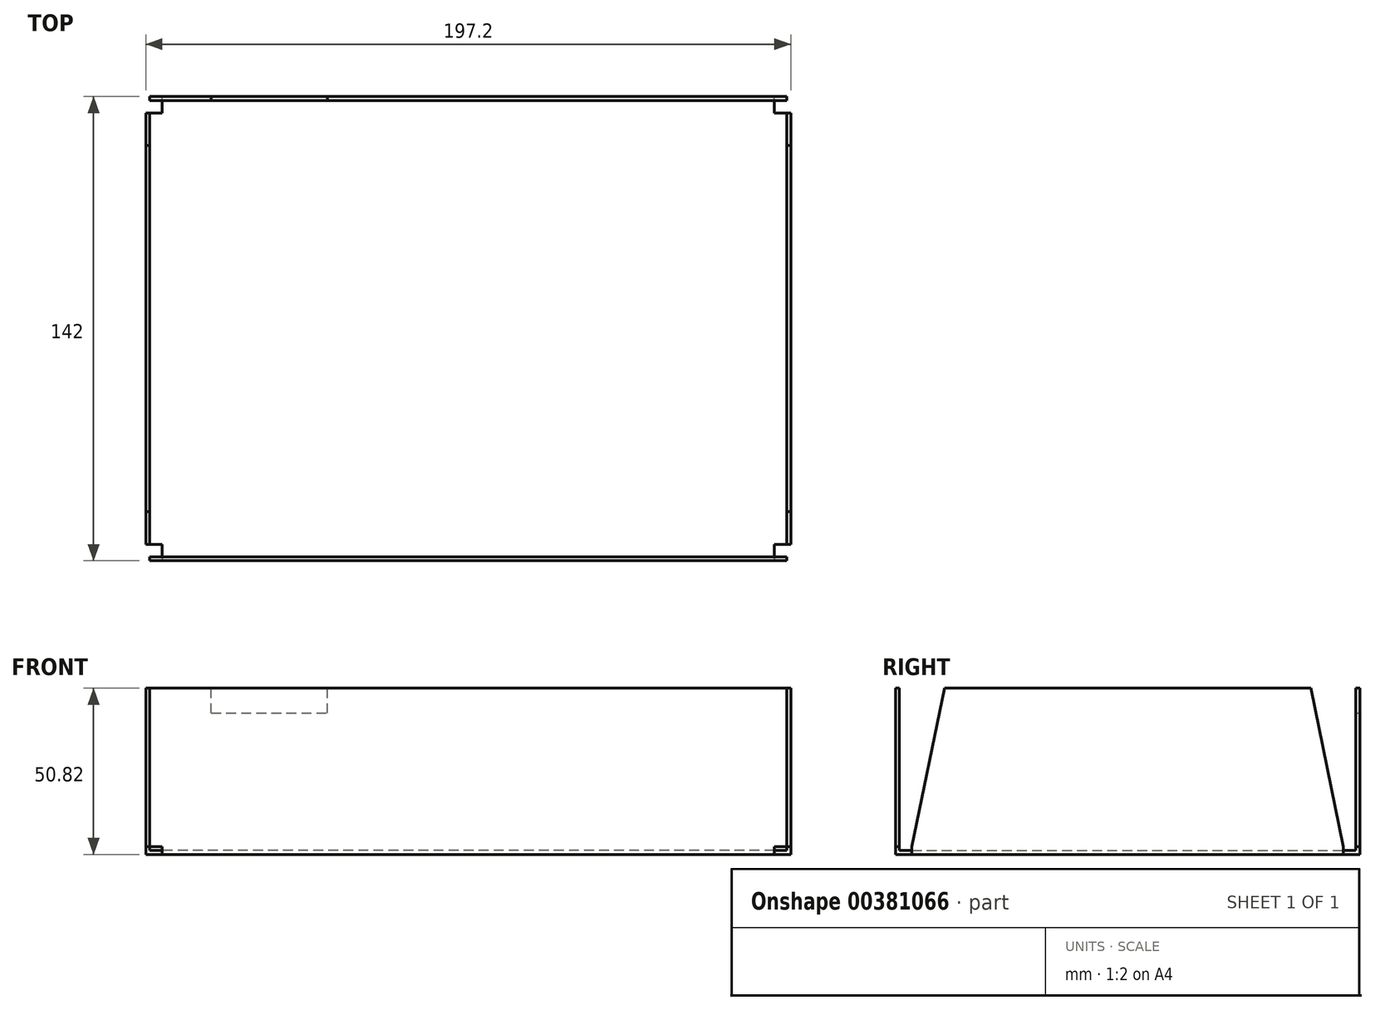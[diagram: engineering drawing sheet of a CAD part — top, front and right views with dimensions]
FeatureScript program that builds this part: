
annotation { "Feature Type Name" : "Feature", "Feature Type Description" : "" }
export const myFeature = defineFeature(function(context is Context, id is Id, definition is map)
    precondition{}
    {
        {
            var Q0;
            Q0=qCreatedBy(makeId("Front.planeOp"),FACE);
            var sketch = newSketch(context, id + "F0", { "sketchPlane" : qUnion([Q0])});
            skLineSegment(sketch, "E0", {"start": v(0, 25.41) * mm, "end": v(-98.6, 25.41) * mm});
            skLineSegment(sketch, "E1", {"start": v(0, 25.41) * mm, "end": v(98.6, 25.41) * mm});
            skLineSegment(sketch, "E2", {"start": v(0, -25.41) * mm, "end": v(-98.6, -25.41) * mm});
            skLineSegment(sketch, "E3", {"start": v(0, -25.41) * mm, "end": v(98.6, -25.41) * mm});
            skLineSegment(sketch, "E4", {"start": v(98.6, 25.41) * mm, "end": v(98.6, -25.41) * mm});
            skLineSegment(sketch, "E5", {"start": v(-98.6, 25.41) * mm, "end": v(-98.6, -25.41) * mm});
            skSolve(sketch);
        }
        {
            var Q0;
            Q0 = qSketchRegion(id + "F0", true);
            extrude(context, id + "F1", {"entities" : qUnion([Q0]), "depth" : 71 * mm, "hasSecondDirection" : true, "secondDirectionOppositeDirection" : true, "secondDirectionDepth" : 71 * mm});
        }
        {
            var Q0;
            Q0=makeQuery(id+"F1.opExtrude","SWEPT_FACE",FACE,{"disambiguationData":[OSD([sQuery(id+"F0.wireOp",EDGE,"E0"),sQuery(id+"F0.wireOp",EDGE,"E1")])]});
            var sketch = newSketch(context, id + "F2", { "sketchPlane" : qUnion([Q0])});
            skLineSegment(sketch, "E6", {"start": v(-97.4, -69.8) * mm, "end": v(-97.4, 69.8) * mm});
            skLineSegment(sketch, "E7", {"start": v(-97.4, 69.8) * mm, "end": v(97.4, 69.8) * mm});
            skLineSegment(sketch, "E8", {"start": v(97.4, 69.8) * mm, "end": v(97.4, -69.8) * mm});
            skLineSegment(sketch, "E9", {"start": v(97.4, -69.8) * mm, "end": v(-97.4, -69.8) * mm});
            skSolve(sketch);
        }
        {
            var Q0;
            Q0 = qSketchRegion(id + "F2", true);
            extrude(context, id + "F3", {"entities" : qUnion([Q0]), "operationType" : NewBodyOperationType.REMOVE, "oppositeDirection" : true, "depth" : (50.82 - 1.2) * mm});
        }
        {
            var Q0;
            Q0=makeQuery(id+"F1.opExtrude","CAP_FACE",FACE,{"disambiguationData":[OSD([sQuery(id+"F0.wireOp",EDGE,"E0"),sQuery(id+"F0.wireOp",EDGE,"E1"),sQuery(id+"F0.wireOp",EDGE,"E2"),sQuery(id+"F0.wireOp",EDGE,"E3"),sQuery(id+"F0.wireOp",EDGE,"E4"),sQuery(id+"F0.wireOp",EDGE,"E5")])],"isStart":true});
            var sketch = newSketch(context, id + "F4", { "sketchPlane" : qUnion([Q0])});
            skLineSegment(sketch, "E10", {"start": v(78.6, 17.8) * mm, "end": v(78.6, 25.41) * mm});
            skLineSegment(sketch, "E11", {"start": v(78.6, 17.8) * mm, "end": v(43.04, 17.8) * mm});
            skLineSegment(sketch, "E12", {"start": v(43.04, 17.8) * mm, "end": v(43.04, 25.41) * mm});
            skSolve(sketch);
        }
        {
            var Q0;
            {var subQ0=sQuery(id+"F4.wireOp",EDGE,"E10");Q0=makeQuery(id+"F4.imprint","IMPRINT",FACE,{"disambiguationData":[TD([[makeQuery(id+"F4.imprint","IMPRINT",EDGE,{"derivedFrom":subQ0}),1.0]])]});}
            extrude(context, id + "F5", {"entities" : qUnion([Q0]), "operationType" : NewBodyOperationType.REMOVE, "oppositeDirection" : true, "depth" : 25 * mm});
        }
        {
            var Q0;
            Q0=makeQuery(id+"F1.opExtrude","SWEPT_FACE",FACE,{"disambiguationData":[OSD([sQuery(id+"F0.wireOp",EDGE,"E4")])]});
            var sketch = newSketch(context, id + "F6", { "sketchPlane" : qUnion([Q0])});
            skLineSegment(sketch, "E13", {"start": v(-71, -25.41) * mm, "end": v(-71, -24.21) * mm, "construction": true});
            skLineSegment(sketch, "E14", {"start": v(-71, -24.21) * mm, "end": v(-66, -24.21) * mm});
            skLineSegment(sketch, "E15", {"start": v(-66, -24.21) * mm, "end": v(-66, -23.01) * mm});
            skLineSegment(sketch, "E16", {"start": v(-66, -23.01) * mm, "end": v(-71, -23.01) * mm});
            skLineSegment(sketch, "E17", {"start": v(-71, -23.01) * mm, "end": v(-71, -24.21) * mm});
            skLineSegment(sketch, "E18", {"start": v(71, -25.41) * mm, "end": v(71, -24.21) * mm, "construction": true});
            skLineSegment(sketch, "E19", {"start": v(66, -24.21) * mm, "end": v(71, -24.21) * mm});
            skLineSegment(sketch, "E20", {"start": v(66, -24.21) * mm, "end": v(66, -23.01) * mm});
            skLineSegment(sketch, "E21", {"start": v(66, -23.01) * mm, "end": v(71, -23.01) * mm});
            skLineSegment(sketch, "E22", {"start": v(71, -23.01) * mm, "end": v(71, -24.21) * mm});
            skSolve(sketch);
        }
        {
            var Q0;
            Q0 = qSketchRegion(id + "F6", true);
            extrude(context, id + "F7", {"entities" : qUnion([Q0]), "operationType" : NewBodyOperationType.REMOVE, "oppositeDirection" : true, "depth" : 5 * mm});
        }
        {
            var Q0;
            Q0=makeQuery(id+"F1.opExtrude","SWEPT_FACE",FACE,{"disambiguationData":[OSD([sQuery(id+"F0.wireOp",EDGE,"E4")])]});
            var sketch = newSketch(context, id + "F8", { "sketchPlane" : qUnion([Q0])});
            skLineSegment(sketch, "E23", {"start": v(-71, -23.01) * mm, "end": v(-69.8, -23.01) * mm});
            skLineSegment(sketch, "E24", {"start": v(-69.8, -23.01) * mm, "end": v(-69.8, 25.41) * mm});
            skLineSegment(sketch, "E25", {"start": v(-69.8, 25.41) * mm, "end": v(-71, 25.41) * mm});
            skLineSegment(sketch, "E26", {"start": v(-71, 25.41) * mm, "end": v(-71, -23.01) * mm});
            skLineSegment(sketch, "E27", {"start": v(71, -23.01) * mm, "end": v(69.8, -23.01) * mm});
            skLineSegment(sketch, "E28", {"start": v(69.8, -23.01) * mm, "end": v(69.8, 25.41) * mm});
            skLineSegment(sketch, "E29", {"start": v(69.8, 25.41) * mm, "end": v(71, 25.41) * mm});
            skLineSegment(sketch, "E30", {"start": v(71, 25.41) * mm, "end": v(71, -23.01) * mm});
            skSolve(sketch);
        }
        {
            var Q0;
            Q0 = qSketchRegion(id + "F8", true);
            extrude(context, id + "F9", {"entities" : qUnion([Q0]), "operationType" : NewBodyOperationType.REMOVE, "oppositeDirection" : true, "depth" : 1.21 * mm});
        }
        {
            var Q0;
            Q0=makeQuery(id+"F1.opExtrude","SWEPT_FACE",FACE,{"disambiguationData":[OSD([sQuery(id+"F0.wireOp",EDGE,"E5")])]});
            var sketch = newSketch(context, id + "F10", { "sketchPlane" : qUnion([Q0])});
            skLineSegment(sketch, "E31", {"start": v(71, -25.41) * mm, "end": v(71, -24.21) * mm, "construction": true});
            skLineSegment(sketch, "E32", {"start": v(71, -24.21) * mm, "end": v(66, -24.21) * mm});
            skLineSegment(sketch, "E33", {"start": v(66, -24.21) * mm, "end": v(66, -23.01) * mm});
            skLineSegment(sketch, "E34", {"start": v(66, -23.01) * mm, "end": v(71, -23.01) * mm});
            skLineSegment(sketch, "E35", {"start": v(71, -23.01) * mm, "end": v(71, -24.21) * mm});
            skLineSegment(sketch, "E36", {"start": v(-71, -25.41) * mm, "end": v(-71, -24.21) * mm, "construction": true});
            skLineSegment(sketch, "E37", {"start": v(-71, -24.21) * mm, "end": v(-66, -24.21) * mm});
            skLineSegment(sketch, "E38", {"start": v(-66, -24.21) * mm, "end": v(-66, -23.01) * mm});
            skLineSegment(sketch, "E39", {"start": v(-66, -23.01) * mm, "end": v(-71, -23.01) * mm});
            skLineSegment(sketch, "E40", {"start": v(-71, -23.01) * mm, "end": v(-71, -24.21) * mm});
            skSolve(sketch);
        }
        {
            var Q0;
            Q0 = qSketchRegion(id + "F10", true);
            extrude(context, id + "F11", {"entities" : qUnion([Q0]), "operationType" : NewBodyOperationType.REMOVE, "oppositeDirection" : true, "depth" : 5 * mm});
        }
        {
            var Q0;
            Q0=makeQuery(id+"F1.opExtrude","SWEPT_FACE",FACE,{"disambiguationData":[OSD([sQuery(id+"F0.wireOp",EDGE,"E5")])]});
            var sketch = newSketch(context, id + "F12", { "sketchPlane" : qUnion([Q0])});
            skLineSegment(sketch, "E41", {"start": v(-71, -23.01) * mm, "end": v(-69.8, -23.01) * mm});
            skLineSegment(sketch, "E42", {"start": v(-69.8, -23.01) * mm, "end": v(-69.8, 25.41) * mm});
            skLineSegment(sketch, "E43", {"start": v(-69.8, 25.41) * mm, "end": v(-71, 25.41) * mm});
            skLineSegment(sketch, "E44", {"start": v(-71, 25.41) * mm, "end": v(-71, -23.01) * mm});
            skLineSegment(sketch, "E45", {"start": v(71, -23.01) * mm, "end": v(69.8, -23.01) * mm});
            skLineSegment(sketch, "E46", {"start": v(69.8, -23.01) * mm, "end": v(69.8, 25.41) * mm});
            skLineSegment(sketch, "E47", {"start": v(69.8, 25.41) * mm, "end": v(71, 25.41) * mm});
            skLineSegment(sketch, "E48", {"start": v(71, 25.41) * mm, "end": v(71, -23.01) * mm});
            skSolve(sketch);
        }
        {
            var Q0;
            Q0 = qSketchRegion(id + "F12", true);
            extrude(context, id + "F13", {"entities" : qUnion([Q0]), "operationType" : NewBodyOperationType.REMOVE, "oppositeDirection" : true, "depth" : 1.21 * mm});
        }
        {
            var Q0;
            Q0=makeQuery(id+"F1.opExtrude","SWEPT_FACE",FACE,{"disambiguationData":[OSD([sQuery(id+"F0.wireOp",EDGE,"E5")])]});
            var sketch = newSketch(context, id + "F14", { "sketchPlane" : qUnion([Q0])});
            skLineSegment(sketch, "E49", {"start": v(-66, 25.41) * mm, "end": v(-56, 25.41) * mm});
            skLineSegment(sketch, "E50", {"start": v(-56, 25.41) * mm, "end": v(-66, -23.01) * mm});
            skLineSegment(sketch, "E51", {"start": v(66, 25.41) * mm, "end": v(56, 25.41) * mm});
            skLineSegment(sketch, "E52", {"start": v(56, 25.41) * mm, "end": v(66, -23.01) * mm});
            skLineSegment(sketch, "E53", {"start": v(-66, 25.41) * mm, "end": v(-69.8, 25.41) * mm});
            skLineSegment(sketch, "E54", {"start": v(-69.8, 25.41) * mm, "end": v(-69.8, -23.01) * mm});
            skLineSegment(sketch, "E55", {"start": v(-69.8, -23.01) * mm, "end": v(-66, -23.01) * mm});
            skLineSegment(sketch, "E56", {"start": v(66, 25.41) * mm, "end": v(69.8, 25.41) * mm});
            skLineSegment(sketch, "E57", {"start": v(69.8, 25.41) * mm, "end": v(69.8, -23.01) * mm});
            skLineSegment(sketch, "E58", {"start": v(69.8, -23.01) * mm, "end": v(66, -23.01) * mm});
            skSolve(sketch);
        }
        {
            var Q0;
            Q0 = qSketchRegion(id + "F14", true);
            extrude(context, id + "F15", {"entities" : qUnion([Q0]), "operationType" : NewBodyOperationType.REMOVE, "endBound" : BoundingType.UP_TO_NEXT, "oppositeDirection" : true, "depth" : 25 * mm});
        }
        {
            var Q0;
            Q0=makeQuery(id+"F1.opExtrude","SWEPT_FACE",FACE,{"disambiguationData":[OSD([sQuery(id+"F0.wireOp",EDGE,"E4")])]});
            var sketch = newSketch(context, id + "F16", { "sketchPlane" : qUnion([Q0])});
            skLineSegment(sketch, "E59", {"start": v(-66, 25.41) * mm, "end": v(-56, 25.41) * mm});
            skLineSegment(sketch, "E60", {"start": v(-56, 25.41) * mm, "end": v(-66, -23.01) * mm});
            skLineSegment(sketch, "E61", {"start": v(-69.8, -23.01) * mm, "end": v(-69.8, 25.41) * mm});
            skLineSegment(sketch, "E62", {"start": v(-69.8, 25.41) * mm, "end": v(-66, 25.41) * mm});
            skLineSegment(sketch, "E63", {"start": v(-69.8, -23.01) * mm, "end": v(-66, -23.01) * mm});
            skLineSegment(sketch, "E64", {"start": v(69.8, -23.01) * mm, "end": v(69.8, 25.41) * mm});
            skLineSegment(sketch, "E65", {"start": v(69.8, 25.41) * mm, "end": v(56, 25.41) * mm});
            skLineSegment(sketch, "E66", {"start": v(56, 25.41) * mm, "end": v(66, -23.01) * mm});
            skLineSegment(sketch, "E67", {"start": v(66, -23.01) * mm, "end": v(69.8, -23.01) * mm});
            skSolve(sketch);
        }
        {
            var Q0;
            Q0 = qSketchRegion(id + "F16", true);
            extrude(context, id + "F17", {"entities" : qUnion([Q0]), "operationType" : NewBodyOperationType.REMOVE, "endBound" : BoundingType.UP_TO_NEXT, "oppositeDirection" : true, "depth" : 25 * mm});
        }
        {
            var Q0;
            Q0=makeQuery(id+"F1.opExtrude","SWEPT_FACE",FACE,{"disambiguationData":[OSD([sQuery(id+"F0.wireOp",EDGE,"E2"),sQuery(id+"F0.wireOp",EDGE,"E3")])]});
            var sketch = newSketch(context, id + "F18", { "sketchPlane" : qUnion([Q0])});
            skLineSegment(sketch, "E68.bottom", {"start": v(-98.6, 71) * mm, "end": v(-93.6, 71) * mm});
            skLineSegment(sketch, "E68.top", {"start": v(-98.6, 66) * mm, "end": v(-93.6, 66) * mm});
            skLineSegment(sketch, "E68.left", {"start": v(-98.6, 71) * mm, "end": v(-98.6, 66) * mm});
            skLineSegment(sketch, "E68.right", {"start": v(-93.6, 71) * mm, "end": v(-93.6, 66) * mm});
            skLineSegment(sketch, "E69.bottom", {"start": v(98.6, 71) * mm, "end": v(93.6, 71) * mm});
            skLineSegment(sketch, "E69.top", {"start": v(98.6, 66) * mm, "end": v(93.6, 66) * mm});
            skLineSegment(sketch, "E69.left", {"start": v(98.6, 71) * mm, "end": v(98.6, 66) * mm});
            skLineSegment(sketch, "E69.right", {"start": v(93.6, 71) * mm, "end": v(93.6, 66) * mm});
            skLineSegment(sketch, "E70.bottom", {"start": v(98.6, -71) * mm, "end": v(93.6, -71) * mm});
            skLineSegment(sketch, "E70.top", {"start": v(98.6, -66) * mm, "end": v(93.6, -66) * mm});
            skLineSegment(sketch, "E70.left", {"start": v(98.6, -71) * mm, "end": v(98.6, -66) * mm});
            skLineSegment(sketch, "E70.right", {"start": v(93.6, -71) * mm, "end": v(93.6, -66) * mm});
            skLineSegment(sketch, "E71.bottom", {"start": v(-98.6, -71) * mm, "end": v(-93.6, -71) * mm});
            skLineSegment(sketch, "E71.top", {"start": v(-98.6, -66) * mm, "end": v(-93.6, -66) * mm});
            skLineSegment(sketch, "E71.left", {"start": v(-98.6, -71) * mm, "end": v(-98.6, -66) * mm});
            skLineSegment(sketch, "E71.right", {"start": v(-93.6, -71) * mm, "end": v(-93.6, -66) * mm});
            skSolve(sketch);
        }
        {
            var Q0;
            Q0=makeQuery(id+"F18.imprint","IMPRINT",FACE,{"disambiguationData":[TD([[makeQuery(id+"F18.imprint","IMPRINT",EDGE,{"derivedFrom":sQuery(id+"F18.wireOp",EDGE,"E71.bottom")}),-1.0]])]});
            var Q1;
            Q1=makeQuery(id+"F18.imprint","IMPRINT",FACE,{"disambiguationData":[TD([[makeQuery(id+"F18.imprint","IMPRINT",EDGE,{"derivedFrom":sQuery(id+"F18.wireOp",EDGE,"E70.bottom")}),-1.0]])]});
            var Q2;
            Q2=makeQuery(id+"F18.imprint","IMPRINT",FACE,{"disambiguationData":[TD([[makeQuery(id+"F18.imprint","IMPRINT",EDGE,{"derivedFrom":sQuery(id+"F18.wireOp",EDGE,"E69.bottom")}),1.0]])]});
            var Q3;
            Q3=makeQuery(id+"F18.imprint","IMPRINT",FACE,{"disambiguationData":[TD([[makeQuery(id+"F18.imprint","IMPRINT",EDGE,{"derivedFrom":sQuery(id+"F18.wireOp",EDGE,"E68.bottom")}),1.0]])]});
            extrude(context, id + "F19", {"entities" : qUnion([Q0, Q1, Q2, Q3]), "operationType" : NewBodyOperationType.REMOVE, "endBound" : BoundingType.UP_TO_NEXT, "oppositeDirection" : true, "depth" : 25 * mm});
        }
    });
